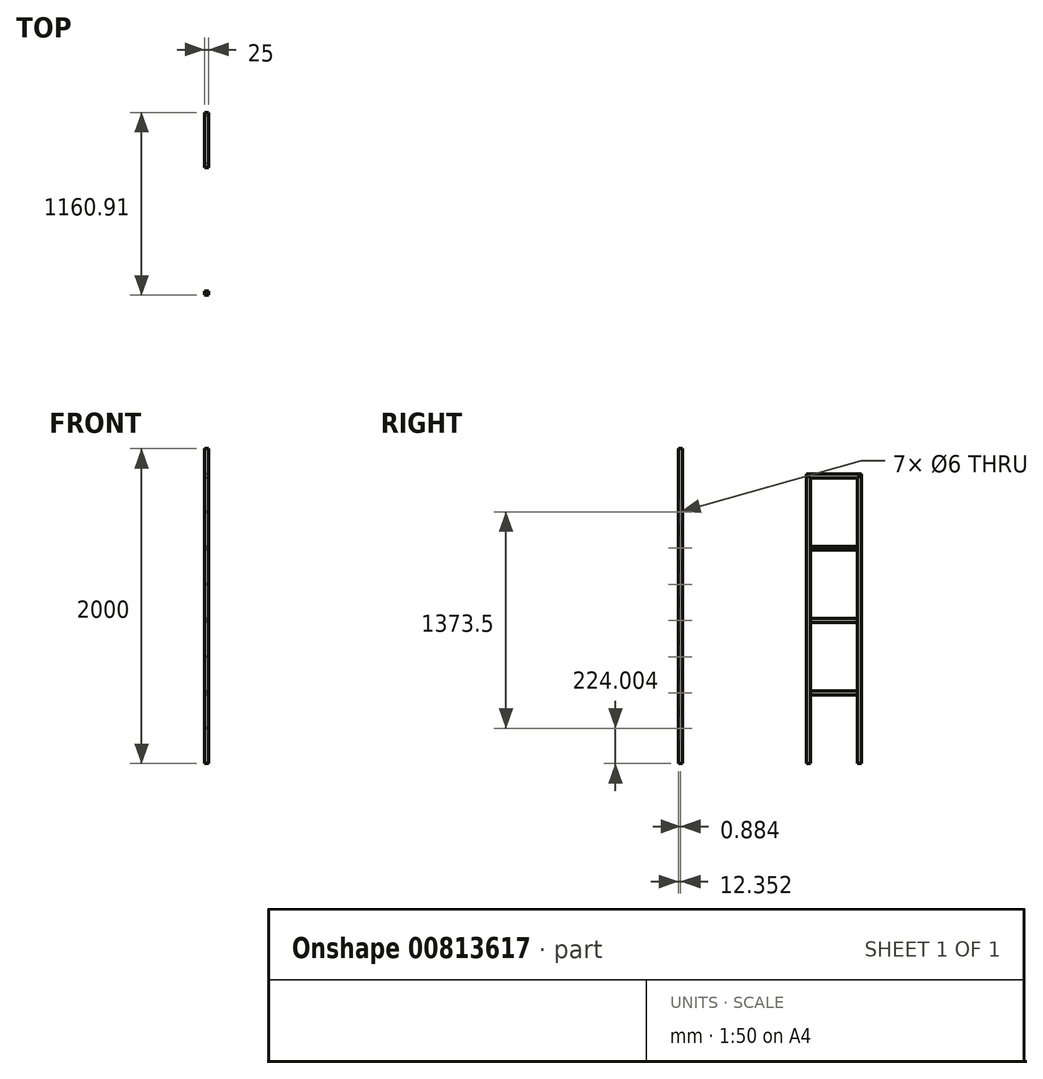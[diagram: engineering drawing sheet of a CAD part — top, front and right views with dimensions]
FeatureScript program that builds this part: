
annotation { "Feature Type Name" : "Feature", "Feature Type Description" : "" }
export const myFeature = defineFeature(function(context is Context, id is Id, definition is map)
    precondition{}
    {
        {
            var Q0;
            Q0=qCreatedBy(makeId("Right.planeOp"),FACE);
            var sketch = newSketch(context, id + "F0", { "sketchPlane" : qUnion([Q0])});
            skLineSegment(sketch, "E0.top", {"start": v(-117.9, -1615.04) * mm, "end": v(-92.9, -1615.04) * mm});
            skLineSegment(sketch, "E0.left", {"start": v(-117.9, 224.96) * mm, "end": v(-117.9, -1615.04) * mm});
            skLineSegment(sketch, "E0.right", {"start": v(-92.9, 199.96) * mm, "end": v(-92.9, -1615.04) * mm});
            skLineSegment(sketch, "E1.bottom", {"start": v(-92.9, 199.96) * mm, "end": v(207.1, 199.96) * mm});
            skLineSegment(sketch, "E1.top", {"start": v(-117.9, 224.96) * mm, "end": v(232.1, 224.96) * mm});
            skLineSegment(sketch, "E2.top", {"start": v(207.1, -1615.04) * mm, "end": v(232.1, -1615.04) * mm});
            skLineSegment(sketch, "E2.left", {"start": v(207.1, 199.96) * mm, "end": v(207.1, -1615.04) * mm});
            skLineSegment(sketch, "E2.right", {"start": v(232.1, 224.96) * mm, "end": v(232.1, -1615.04) * mm});
            skLineSegment(sketch, "E3", {"start": v(-92.9, 199.96) * mm, "end": v(-117.9, 224.96) * mm});
            skLineSegment(sketch, "E4", {"start": v(232.1, 224.96) * mm, "end": v(207.1, 199.96) * mm});
            skPoint(sketch, "E5.orphan", {"position": v(-92.9, 224.96) * mm});
            skPoint(sketch, "E6.orphan", {"position": v(-117.9, 197.1) * mm});
            skPoint(sketch, "E7.orphan", {"position": v(232.1, 199.96) * mm});
            skLineSegment(sketch, "E8.bottom", {"start": v(-92.9, -1155.04) * mm, "end": v(207.1, -1155.04) * mm});
            skLineSegment(sketch, "E8.top", {"start": v(-92.9, -1180.04) * mm, "end": v(207.1, -1180.04) * mm});
            skLineSegment(sketch, "E8.left", {"start": v(-92.9, -1155.04) * mm, "end": v(-92.9, -1180.04) * mm});
            skLineSegment(sketch, "E8.right", {"start": v(207.1, -1155.04) * mm, "end": v(207.1, -1180.04) * mm});
            skLineSegment(sketch, "E9.bottom", {"start": v(-92.9, -695.04) * mm, "end": v(207.1, -695.04) * mm});
            skLineSegment(sketch, "E9.top", {"start": v(-92.9, -720.04) * mm, "end": v(207.1, -720.04) * mm});
            skLineSegment(sketch, "E9.left", {"start": v(-92.9, -695.04) * mm, "end": v(-92.9, -720.04) * mm});
            skLineSegment(sketch, "E9.right", {"start": v(207.1, -695.04) * mm, "end": v(207.1, -720.04) * mm});
            skLineSegment(sketch, "E10.bottom", {"start": v(-92.9, -260.04) * mm, "end": v(207.1, -260.04) * mm});
            skLineSegment(sketch, "E10.top", {"start": v(-92.9, -235.04) * mm, "end": v(207.1, -235.04) * mm});
            skLineSegment(sketch, "E10.left", {"start": v(-92.9, -260.04) * mm, "end": v(-92.9, -235.04) * mm});
            skLineSegment(sketch, "E10.right", {"start": v(207.1, -260.04) * mm, "end": v(207.1, -235.04) * mm});
            skPoint(sketch, "E11", {"position": v(-105.24, -247.54) * mm});
            skPoint(sketch, "E11.positionSnap0", {"position": v(-92.9, -247.54) * mm});
            skPoint(sketch, "E12", {"position": v(-105.24, -17.54) * mm});
            skPoint(sketch, "E13", {"position": v(-105.24, -477.54) * mm});
            skPoint(sketch, "E14", {"position": v(-105.4, -707.54) * mm});
            skPoint(sketch, "E14.positionSnap0", {"position": v(-92.9, -707.54) * mm});
            skPoint(sketch, "E15", {"position": v(-105.4, -1167.54) * mm});
            skPoint(sketch, "E15.positionSnap0", {"position": v(-92.9, -1167.54) * mm});
            skPoint(sketch, "E16", {"position": v(-105.4, -1391.04) * mm});
            skPoint(sketch, "E17", {"position": v(-106.12, -937.54) * mm});
            skLineSegment(sketch, "E18", {"start": v(-510.84, 419.3) * mm, "end": v(-510.84, -1767.45) * mm});
            skLineSegment(sketch, "E19.MirrorCS", {"start": v(-903.8, 224.96) * mm, "end": v(-903.8, -1615.04) * mm});
            skLineSegment(sketch, "E20.MirrorCS", {"start": v(-928.8, 384.96) * mm, "end": v(-928.8, -1615.04) * mm});
            skPoint(sketch, "E21.MirrorP", {"position": v(-916.45, -477.54) * mm});
            skPoint(sketch, "E22.MirrorP", {"position": v(-916.45, -247.54) * mm});
            skPoint(sketch, "E23.MirrorP", {"position": v(-916.45, -17.54) * mm});
            skLineSegment(sketch, "E24.MirrorCS", {"start": v(-903.8, 384.96) * mm, "end": v(-903.8, -1615.04) * mm});
            skLineSegment(sketch, "E25.MirrorCS", {"start": v(-903.8, -1615.04) * mm, "end": v(-928.8, -1615.04) * mm});
            skPoint(sketch, "E26.MirrorP", {"position": v(-916.3, -1391.04) * mm});
            skPoint(sketch, "E27.MirrorP", {"position": v(-916.3, -1167.54) * mm});
            skPoint(sketch, "E28.MirrorP", {"position": v(-915.56, -937.54) * mm});
            skPoint(sketch, "E29.MirrorP", {"position": v(-916.3, -707.54) * mm});
            skLineSegment(sketch, "E30", {"start": v(-928.8, 384.96) * mm, "end": v(-903.8, 384.96) * mm});
            skPoint(sketch, "E31.MirrorCS.end.orphan", {"position": v(-903.8, 224.96) * mm});
            skPoint(sketch, "E31.MirrorCS.start.orphan", {"position": v(-928.8, 199.96) * mm});
            skCircle(sketch, "E32", {"center": v(-916.45, -17.54) * mm, "radius": 3 * mm});
            skCircle(sketch, "E33", {"center": v(-916.45, -247.54) * mm, "radius": 3 * mm});
            skCircle(sketch, "E34", {"center": v(-916.45, -477.54) * mm, "radius": 3 * mm});
            skCircle(sketch, "E35", {"center": v(-916.3, -707.54) * mm, "radius": 3 * mm});
            skCircle(sketch, "E36", {"center": v(-915.56, -937.54) * mm, "radius": 3 * mm});
            skCircle(sketch, "E37", {"center": v(-916.3, -1167.54) * mm, "radius": 3 * mm});
            skCircle(sketch, "E38", {"center": v(-916.3, -1391.04) * mm, "radius": 3 * mm});
            skSolve(sketch);
        }
        {
            var Q0;
            {var subQ4=sQuery(id+"F0.wireOp",EDGE,"E0.top");Q0=makeQuery(id+"F0.imprint","IMPRINT",FACE,{"disambiguationData":[TD([[makeQuery(id+"F0.imprint","IMPRINT",EDGE,{"derivedFrom":subQ4}),1.0]])]});}
            var Q1;
            {var subQ5=sQuery(id+"F0.wireOp",EDGE,"E2.top");Q1=makeQuery(id+"F0.imprint","IMPRINT",FACE,{"disambiguationData":[TD([[makeQuery(id+"F0.imprint","IMPRINT",EDGE,{"derivedFrom":subQ5}),1.0]])]});}
            var Q2;
            Q2=makeQuery(id+"F0.imprint","IMPRINT",FACE,{"disambiguationData":[TD([[makeQuery(id+"F0.imprint","IMPRINT",EDGE,{"derivedFrom":sQuery(id+"F0.wireOp",EDGE,"E20.MirrorCS")}),1.0]])]});
            extrude(context, id + "F1", {"entities" : qUnion([Q0, Q1, Q2]), "depth" : 25 * mm, "offsetDistance" : 25 * mm});
        }
        {
            var Q0;
            Q0=makeQuery(id+"F0.imprint","IMPRINT",FACE,{"disambiguationData":[TD([[makeQuery(id+"F0.imprint","IMPRINT",EDGE,{"derivedFrom":sQuery(id+"F0.wireOp",EDGE,"E1.bottom")}),1.0]])]});
            var Q1;
            Q1=makeQuery(id+"F0.imprint","IMPRINT",FACE,{"disambiguationData":[TD([[makeQuery(id+"F0.imprint","IMPRINT",EDGE,{"derivedFrom":sQuery(id+"F0.wireOp",EDGE,"E10.bottom")}),1.0]])]});
            var Q2;
            Q2=makeQuery(id+"F0.imprint","IMPRINT",FACE,{"disambiguationData":[TD([[makeQuery(id+"F0.imprint","IMPRINT",EDGE,{"derivedFrom":sQuery(id+"F0.wireOp",EDGE,"E9.bottom")}),-1.0]])]});
            var Q3;
            Q3=makeQuery(id+"F0.imprint","IMPRINT",FACE,{"disambiguationData":[TD([[makeQuery(id+"F0.imprint","IMPRINT",EDGE,{"derivedFrom":sQuery(id+"F0.wireOp",EDGE,"E8.bottom")}),-1.0]])]});
            extrude(context, id + "F2", {"entities" : qUnion([Q0, Q1, Q2, Q3]), "depth" : 25 * mm, "offsetDistance" : 25 * mm});
        }
    });
